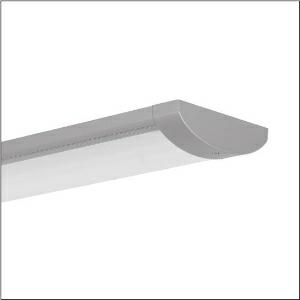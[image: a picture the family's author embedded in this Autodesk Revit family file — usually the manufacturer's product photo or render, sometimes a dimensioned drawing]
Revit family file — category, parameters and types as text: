
# Revit family: tv_20_5xa86172n0a
name_source: partatom
category: Lighting Fixtures
units: mm (PartAtom-declared; Revit-internal decimal feet)

## family parameters
Cut with Voids When Loaded = No
Host = Face
Light Source = No
Part Type = Normal
Room Calculation Point = No
Round Connector Dimension = Use Diameter
Shared = No

## types (1)
- TV 20 (1 x LED 4000K / CRI = 80 (unbekannt), 2130 lm, 4000K)
    Apparent Load = 21 VA
    CIE Flux Codes = 48 78 95 99 100
    Color Rendering = 80
    Color Temperature = 4000K
    Default Elevation = 1800 mm
    Description = TV 20, vandal-proof luminaire, primary light control with specular reflector, of aluminium, matt, primary optical cover: enclosure, of PC, frosted, light emission: direct distribution, primary light characteristic: symmetric, installation type: surface-mounted, LED, rated luminous flux: 2.130lm, luminous efficacy: 101lm/W, light colour: 840, colour temperature: 4000K, control gear: ON/OFF, mains connection: 230V, AC, 50Hz, rated input power: 21W, luminaire housing, of aluminium, coated, Siteco® metallic grey (DB 702S), with wall and ceiling fixing element, length: 705mm, width: 260mm, height: 70mm, mounting height: 2.5..4.0m, protection rating (complete): IP65, insulation class (complete): insulation class I (protective earthing), certification: CE, protection symbol: F, impact resistance: 2x IK10, standard: EN 60598, packaging unit: 1 piece
    Height = 70 mm
    Lamp = 1 x LED 4000K / CRI >= 80 (unbekannt)
    Lamp Light Flux = 2130 lm
    Lamp count = 1
    Length = 705 mm
    Luminous efficacy = 101 lm/W
    Manufacturer = Siteco
    ModVariant = No
    Model = 5XA86172N0A
    Mounting Place = Ceiling
    Mounting Type = Surface mounted
    Number of Poles = 1
    OnlyDefault = Yes
    Power Factor = 1
    Product Name = TV 20
    Product group = vandal-proof luminaire
    ProductGroupID = 309
    Protection Class = Protection class I
    Protection Degree = IP 65
    RLX_Detail_Level = 1
    RLX_Emergency_Light_Flux = 0 lm
    RLX_Emergency_Type = 0
    RLX_Emergency_Type_DB = No
    RlxData = <blob elided: 34197 chars, md5=81cfe485>
    Socket = socket
    Standby Power = 0 W
    System Light Flux = 2130 lm
    System Power = 21 W
    Type Comments = Product without accessories
    Type Image = l_1004809.jpg
    URL = http://relux.com
    VarID = ---
    Voltage = 0 V
    Weight = 0.00 kg
    Width = 260 mm

## geometry (parser evidence)
native form markers: Blend x4, Sweep x11
no freeform markers — native parametric forms only
